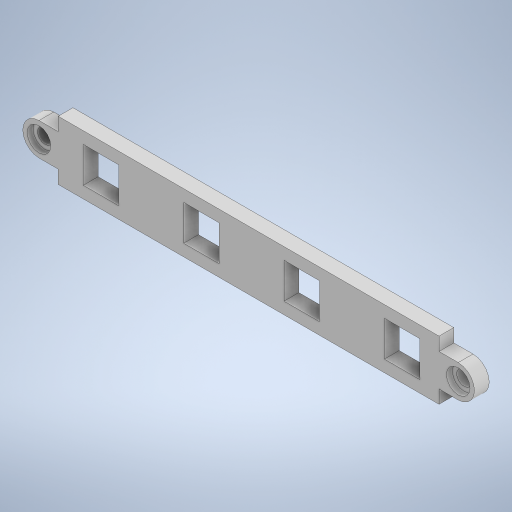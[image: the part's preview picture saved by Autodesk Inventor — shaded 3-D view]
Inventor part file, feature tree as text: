
AUTODESK INVENTOR PART (.ipt)
format: ipt  version: 2023 (Build 270158000, 158)  size: 290,816 bytes
history: native  units: mm
features: extrude x3, sketch x3, other x1
ambient origin geometry x8: Origin, YZ Plane, XZ Plane, XY Plane, X Axis, Y Axis, Z Axis, Center Point
bodies: Body1 (feature_tree)
feature tree (7):
  other  "솔리드1"
  extrude  "돌출1"  Depth=64.5mm
  extrude  "돌출2"  Depth=10.0mm
  extrude  "돌출3"  Depth=5.5mm
  sketch  "스케치1"
  sketch  "스케치2"
  sketch  "스케치3"
